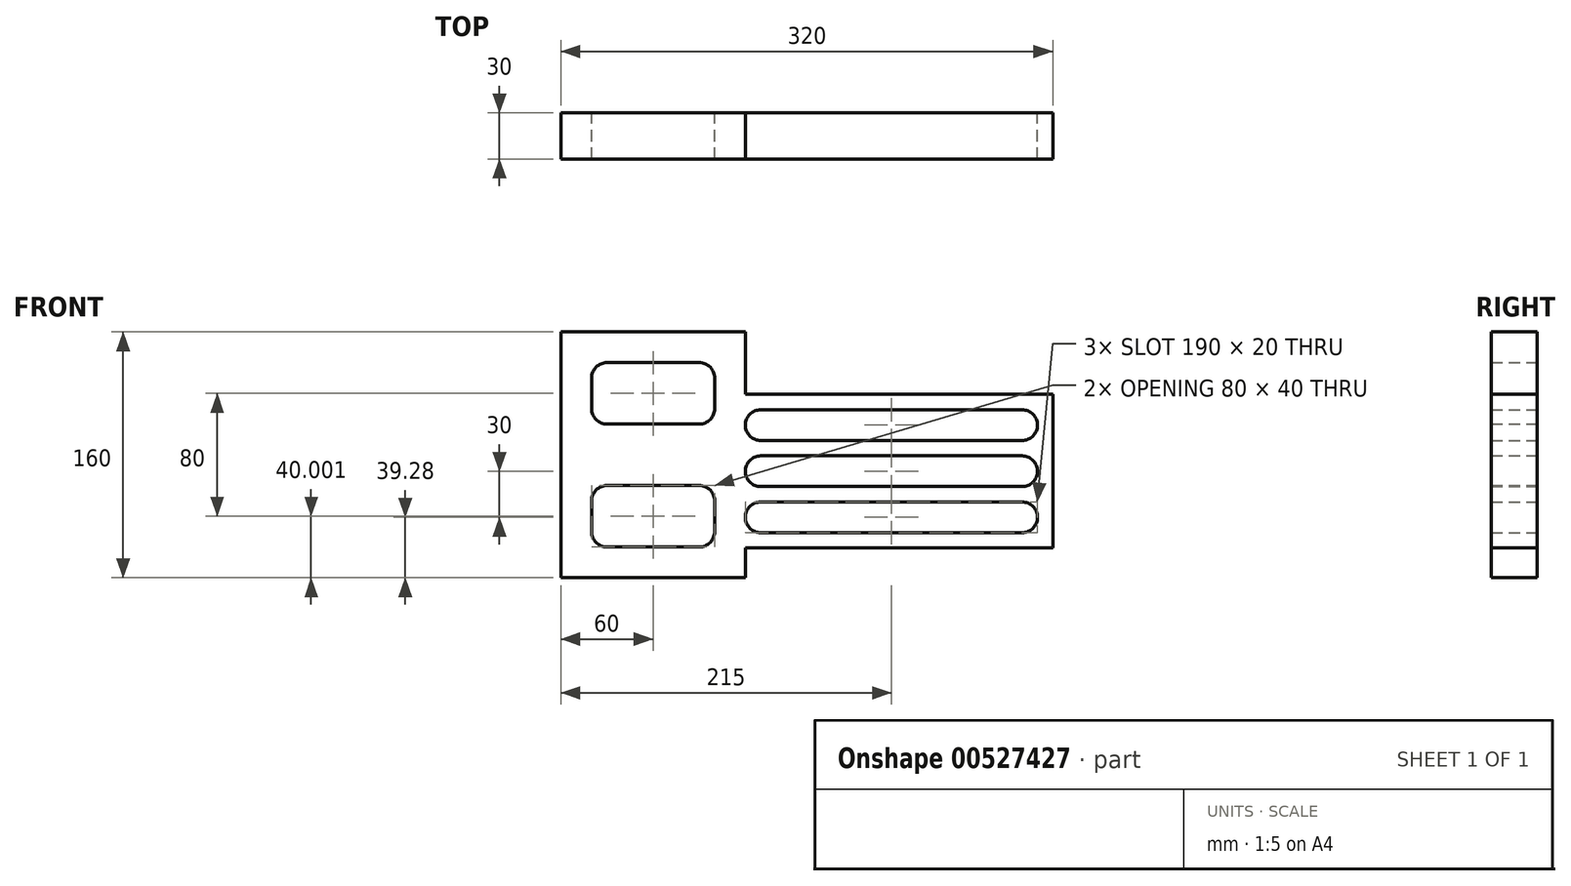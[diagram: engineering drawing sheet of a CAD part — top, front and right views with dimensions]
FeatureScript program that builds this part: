
annotation { "Feature Type Name" : "Feature", "Feature Type Description" : "" }
export const myFeature = defineFeature(function(context is Context, id is Id, definition is map)
    precondition{}
    {
        {
            var Q0;
            Q0=qCreatedBy(makeId("Front.planeOp"),FACE);
            var sketch = newSketch(context, id + "F0", { "sketchPlane" : qUnion([Q0])});
            skLineSegment(sketch, "E0", {"start": v(0, 0) * mm, "end": v(-200, 0) * mm});
            skLineSegment(sketch, "E1", {"start": v(0, 0) * mm, "end": v(0, -100) * mm});
            skLineSegment(sketch, "E2", {"start": v(0, -100) * mm, "end": v(-200, -100) * mm});
            skLineSegment(sketch, "E3", {"start": v(-200, 0) * mm, "end": v(-200, 40.72) * mm});
            skLineSegment(sketch, "E4", {"start": v(-200, 40.72) * mm, "end": v(-320, 40.72) * mm});
            skLineSegment(sketch, "E5", {"start": v(-320, 40.72) * mm, "end": v(-320, -119.28) * mm});
            skLineSegment(sketch, "E6", {"start": v(-320, -119.28) * mm, "end": v(-200, -119.28) * mm});
            skLineSegment(sketch, "E7", {"start": v(-200, -119.28) * mm, "end": v(-200, -100) * mm});
            skLineSegment(sketch, "E8.bottom", {"start": v(-290, 20.72) * mm, "end": v(-230, 20.72) * mm});
            skLineSegment(sketch, "E8.top", {"start": v(-290, -19.28) * mm, "end": v(-230, -19.28) * mm});
            skLineSegment(sketch, "E8.left", {"start": v(-300, 10.72) * mm, "end": v(-300, -9.28) * mm});
            skLineSegment(sketch, "E8.right", {"start": v(-220, 10.72) * mm, "end": v(-220, -9.28) * mm});
            skLineSegment(sketch, "E9.bottom", {"start": v(-290, -59.28) * mm, "end": v(-230, -59.28) * mm});
            skLineSegment(sketch, "E9.top", {"start": v(-290, -99.28) * mm, "end": v(-230, -99.28) * mm});
            skLineSegment(sketch, "E9.left", {"start": v(-300, -69.28) * mm, "end": v(-300, -89.28) * mm});
            skLineSegment(sketch, "E9.right", {"start": v(-220, -69.28) * mm, "end": v(-220, -89.28) * mm});
            skLineSegment(sketch, "E10.bottom", {"start": v(-190, -10) * mm, "end": v(-20, -10) * mm});
            skLineSegment(sketch, "E10.top", {"start": v(-190, -30) * mm, "end": v(-20, -30) * mm});
            skLineSegment(sketch, "E10.right", {"start": v(-10, -20) * mm, "end": v(-10, -20) * mm});
            skLineSegment(sketch, "E11.bottom", {"start": v(-190, -40) * mm, "end": v(-20, -40) * mm});
            skLineSegment(sketch, "E11.top", {"start": v(-190, -60) * mm, "end": v(-20, -60) * mm});
            skLineSegment(sketch, "E11.left", {"start": v(-200, -50) * mm, "end": v(-200, -50) * mm});
            skLineSegment(sketch, "E11.right", {"start": v(-10, -50) * mm, "end": v(-10, -50) * mm});
            skLineSegment(sketch, "E12.bottom", {"start": v(-190, -70) * mm, "end": v(-20, -70) * mm});
            skLineSegment(sketch, "E12.top", {"start": v(-190, -90) * mm, "end": v(-20, -90) * mm});
            skLineSegment(sketch, "E12.left", {"start": v(-200, -80) * mm, "end": v(-200, -80) * mm});
            skLineSegment(sketch, "E12.right", {"start": v(-10, -80) * mm, "end": v(-10, -80) * mm});
            skLineSegment(sketch, "E13", {"start": v(-200, -20) * mm, "end": v(-200, -20) * mm});
            skPoint(sketch, "E14.visualSharp", {"position": v(-300, 20.72) * mm});
            skArc(sketch, "E14.filletArc", {"start": v(-290, 20.72) * mm, "mid": v(-297.07, 17.8) * mm, "end": v(-300, 10.72) * mm});
            skPoint(sketch, "E15.visualSharp", {"position": v(-300, -19.28) * mm});
            skArc(sketch, "E15.filletArc", {"start": v(-300, -9.28) * mm, "mid": v(-297.07, -16.35) * mm, "end": v(-290, -19.28) * mm});
            skPoint(sketch, "E16.visualSharp", {"position": v(-220, -19.28) * mm});
            skArc(sketch, "E16.filletArc", {"start": v(-230, -19.28) * mm, "mid": v(-222.93, -16.35) * mm, "end": v(-220, -9.28) * mm});
            skPoint(sketch, "E17.visualSharp", {"position": v(-220, 20.72) * mm});
            skArc(sketch, "E17.filletArc", {"start": v(-220, 10.72) * mm, "mid": v(-222.93, 17.8) * mm, "end": v(-230, 20.72) * mm});
            skPoint(sketch, "E18.visualSharp", {"position": v(-300, -59.28) * mm});
            skArc(sketch, "E18.filletArc", {"start": v(-290, -59.28) * mm, "mid": v(-297.07, -62.2) * mm, "end": v(-300, -69.28) * mm});
            skPoint(sketch, "E19.visualSharp", {"position": v(-300, -99.28) * mm});
            skArc(sketch, "E19.filletArc", {"start": v(-300, -89.28) * mm, "mid": v(-297.07, -96.35) * mm, "end": v(-290, -99.28) * mm});
            skPoint(sketch, "E20.visualSharp", {"position": v(-220, -99.28) * mm});
            skArc(sketch, "E20.filletArc", {"start": v(-230, -99.28) * mm, "mid": v(-222.93, -96.35) * mm, "end": v(-220, -89.28) * mm});
            skPoint(sketch, "E21.visualSharp", {"position": v(-220, -59.28) * mm});
            skArc(sketch, "E21.filletArc", {"start": v(-220, -69.28) * mm, "mid": v(-222.93, -62.2) * mm, "end": v(-230, -59.28) * mm});
            skPoint(sketch, "E22.visualSharp", {"position": v(-200, -10) * mm});
            skArc(sketch, "E22.filletArc", {"start": v(-190, -10) * mm, "mid": v(-197.07, -12.93) * mm, "end": v(-200, -20) * mm});
            skPoint(sketch, "E23.visualSharp", {"position": v(-200, -30) * mm});
            skArc(sketch, "E23.filletArc", {"start": v(-200, -20) * mm, "mid": v(-197.07, -27.07) * mm, "end": v(-190, -30) * mm});
            skPoint(sketch, "E24.visualSharp", {"position": v(-10, -30) * mm});
            skArc(sketch, "E24.filletArc", {"start": v(-20, -30) * mm, "mid": v(-12.93, -27.07) * mm, "end": v(-10, -20) * mm});
            skPoint(sketch, "E25.visualSharp", {"position": v(-10, -10) * mm});
            skArc(sketch, "E25.filletArc", {"start": v(-10, -20) * mm, "mid": v(-12.93, -12.93) * mm, "end": v(-20, -10) * mm});
            skPoint(sketch, "E26.visualSharp", {"position": v(-10, -40) * mm});
            skArc(sketch, "E26.filletArc", {"start": v(-10, -50) * mm, "mid": v(-12.93, -42.93) * mm, "end": v(-20, -40) * mm});
            skPoint(sketch, "E27.visualSharp", {"position": v(-10, -60) * mm});
            skArc(sketch, "E27.filletArc", {"start": v(-20, -60) * mm, "mid": v(-12.93, -57.07) * mm, "end": v(-10, -50) * mm});
            skPoint(sketch, "E28.visualSharp", {"position": v(-200, -60) * mm});
            skArc(sketch, "E28.filletArc", {"start": v(-200, -50) * mm, "mid": v(-197.07, -57.07) * mm, "end": v(-190, -60) * mm});
            skPoint(sketch, "E29.visualSharp", {"position": v(-200, -40) * mm});
            skArc(sketch, "E29.filletArc", {"start": v(-190, -40) * mm, "mid": v(-197.07, -42.93) * mm, "end": v(-200, -50) * mm});
            skPoint(sketch, "E30.visualSharp", {"position": v(-200, -70) * mm});
            skArc(sketch, "E30.filletArc", {"start": v(-190, -70) * mm, "mid": v(-197.07, -72.93) * mm, "end": v(-200, -80) * mm});
            skPoint(sketch, "E31.visualSharp", {"position": v(-200, -90) * mm});
            skArc(sketch, "E31.filletArc", {"start": v(-200, -80) * mm, "mid": v(-197.07, -87.07) * mm, "end": v(-190, -90) * mm});
            skPoint(sketch, "E32.visualSharp", {"position": v(-10, -90) * mm});
            skArc(sketch, "E32.filletArc", {"start": v(-20, -90) * mm, "mid": v(-12.93, -87.07) * mm, "end": v(-10, -80) * mm});
            skPoint(sketch, "E33.visualSharp", {"position": v(-10, -70) * mm});
            skArc(sketch, "E33.filletArc", {"start": v(-10, -80) * mm, "mid": v(-12.93, -72.93) * mm, "end": v(-20, -70) * mm});
            skSolve(sketch);
        }
        {
            var Q0;
            Q0 = qSketchRegion(id + "F0", true);
            extrude(context, id + "F1", {"entities" : qUnion([Q0]), "depth" : 30 * mm, "offsetDistance" : 25 * mm});
        }
    });
